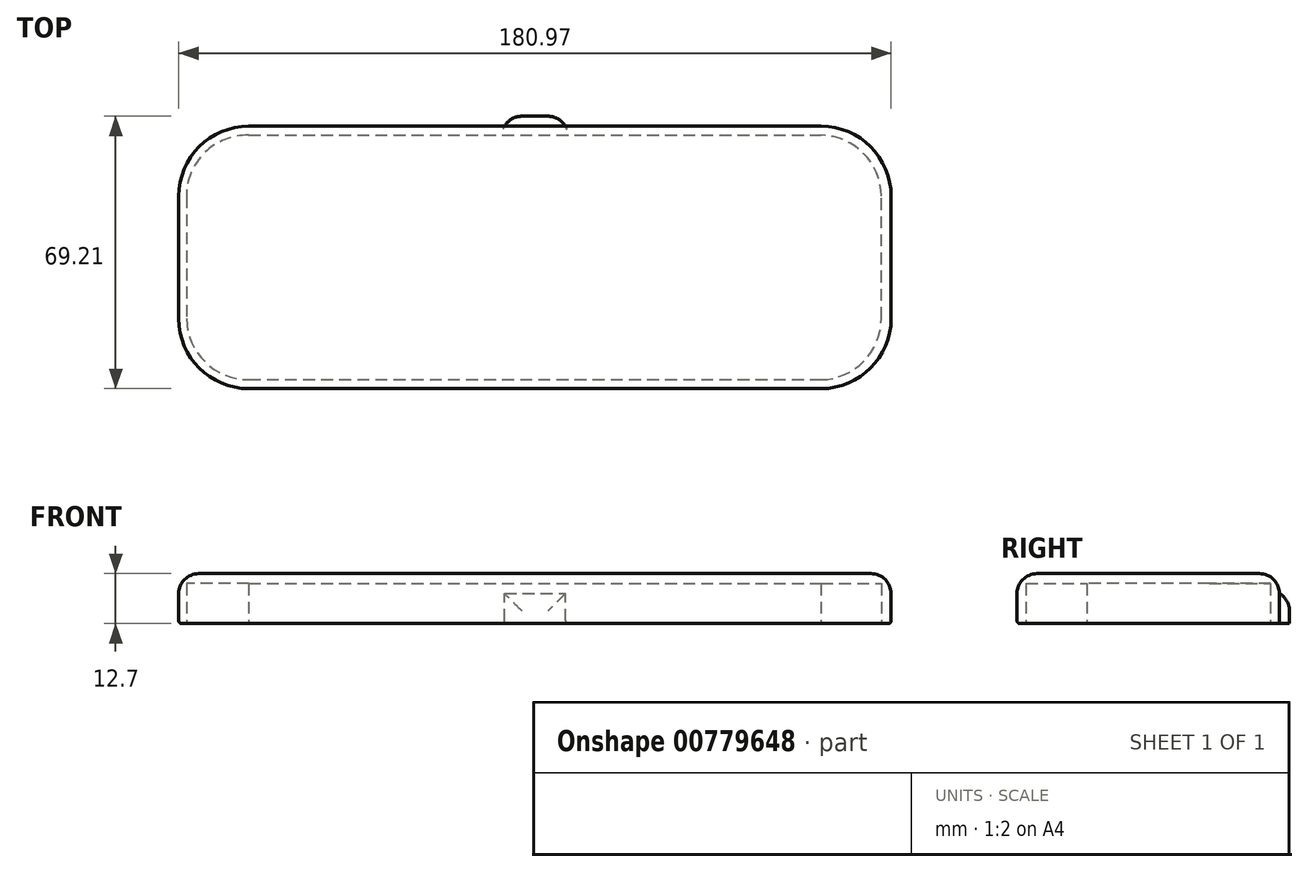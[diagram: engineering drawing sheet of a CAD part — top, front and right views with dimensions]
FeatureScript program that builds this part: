
annotation { "Feature Type Name" : "Feature", "Feature Type Description" : "" }
export const myFeature = defineFeature(function(context is Context, id is Id, definition is map)
    precondition{}
    {
        {
            var Q0;
            Q0=qCreatedBy(makeId("Top.planeOp"),FACE);
            var sketch = newSketch(context, id + "F0", { "sketchPlane" : qUnion([Q0])});
            skLineSegment(sketch, "E0.bottom", {"start": v(-69.58, 3.8) * mm, "end": v(111.4, 3.8) * mm});
            skLineSegment(sketch, "E0.top", {"start": v(-69.58, 70.48) * mm, "end": v(111.4, 70.48) * mm});
            skLineSegment(sketch, "E0.left", {"start": v(-69.58, 3.8) * mm, "end": v(-69.58, 70.48) * mm});
            skLineSegment(sketch, "E0.right", {"start": v(111.4, 3.8) * mm, "end": v(111.4, 70.48) * mm});
            skSolve(sketch);
        }
        {
            var Q0;
            Q0 = qSketchRegion(id + "F0", true);
            extrude(context, id + "F1", {"entities" : qUnion([Q0]), "depth" : 12.7 * mm, "offsetDistance" : 25.4 * mm});
        }
        {
            var Q0;
            Q0=makeQuery(id+"F1.opExtrude","SWEPT_EDGE",EDGE,{"disambiguationData":[OSD([sQuery(id+"F0.wireOp",EDGE,"E0.bottom"),sQuery(id+"F0.wireOp",EDGE,"E0.left")])]});
            var Q1;
            Q1=makeQuery(id+"F1.opExtrude","SWEPT_EDGE",EDGE,{"disambiguationData":[OSD([sQuery(id+"F0.wireOp",EDGE,"E0.bottom"),sQuery(id+"F0.wireOp",EDGE,"E0.right")])]});
            var Q2;
            Q2=makeQuery(id+"F1.opExtrude","SWEPT_EDGE",EDGE,{"disambiguationData":[OSD([sQuery(id+"F0.wireOp",EDGE,"E0.top"),sQuery(id+"F0.wireOp",EDGE,"E0.right")])]});
            var Q3;
            Q3=makeQuery(id+"F1.opExtrude","SWEPT_EDGE",EDGE,{"disambiguationData":[OSD([sQuery(id+"F0.wireOp",EDGE,"E0.top"),sQuery(id+"F0.wireOp",EDGE,"E0.left")])]});
            fillet(context, id + "F2", {"entities" : qUnion([Q0, Q1, Q2, Q3]), "radius" : 17.78 * mm, "tangentPropagation" : true, "allowEdgeOverflow" : false});
        }
        {
            var Q0;
            Q0=makeQuery(id+"F1.opExtrude","CAP_EDGE",EDGE,{"disambiguationData":[OSD([sQuery(id+"F0.wireOp",EDGE,"E0.bottom")])],"isStart":false});
            fillet(context, id + "F3", {"entities" : qUnion([Q0]), "radius" : 5.08 * mm, "tangentPropagation" : true, "allowEdgeOverflow" : false});
        }
        {
            var Q0;
            Q0=makeQuery(id+"F1.opExtrude","CAP_FACE",FACE,{"disambiguationData":[OSD([sQuery(id+"F0.wireOp",EDGE,"E0.bottom"),sQuery(id+"F0.wireOp",EDGE,"E0.top"),sQuery(id+"F0.wireOp",EDGE,"E0.left"),sQuery(id+"F0.wireOp",EDGE,"E0.right")])],"isStart":true});
            var sketch = newSketch(context, id + "F4", { "sketchPlane" : qUnion([Q0])});
            skLineSegment(sketch, "E1.bottom", {"start": v(-49.9, -68.2) * mm, "end": v(91.7, -68.2) * mm});
            skLineSegment(sketch, "E1.top", {"start": v(-49.9, -6.1) * mm, "end": v(91.7, -6.1) * mm});
            skLineSegment(sketch, "E1.left", {"start": v(-49.9, -68.2) * mm, "end": v(-49.9, -6.1) * mm});
            skLineSegment(sketch, "E1.right", {"start": v(91.7, -68.2) * mm, "end": v(91.7, -6.1) * mm});
            skPoint(sketch, "E1.middle", {"position": v(20.9, -37.14) * mm});
            skPoint(sketch, "E1.middle.positionSnap0", {"position": v(-69.58, -37.14) * mm});
            skPoint(sketch, "E1.middle.positionSnap1", {"position": v(20.9, -70.48) * mm});
            skPoint(sketch, "E1.centerSnap0", {"position": v(-69.58, -37.14) * mm});
            skPoint(sketch, "E1.centerSnap1", {"position": v(20.9, -70.48) * mm});
            skSolve(sketch);
        }
        {
            var Q0;
            Q0=makeQuery(id+"F4.imprint","IMPRINT",FACE,{"disambiguationData":[TD([[makeQuery(id+"F4.imprint","IMPRINT",EDGE,{"derivedFrom":sQuery(id+"F4.wireOp",EDGE,"E1.bottom")}),1.0]])]});
            extrude(context, id + "F5", {"entities" : qUnion([Q0]), "operationType" : NewBodyOperationType.REMOVE, "oppositeDirection" : true, "depth" : 10.16 * mm, "offsetDistance" : 25.4 * mm});
        }
        {
            var Q0;
            Q0=makeQuery(id+"F1.opExtrude","CAP_FACE",FACE,{"disambiguationData":[OSD([sQuery(id+"F0.wireOp",EDGE,"E0.bottom"),sQuery(id+"F0.wireOp",EDGE,"E0.top"),sQuery(id+"F0.wireOp",EDGE,"E0.left"),sQuery(id+"F0.wireOp",EDGE,"E0.right")])],"isStart":true});
            var sketch = newSketch(context, id + "F6", { "sketchPlane" : qUnion([Q0])});
            skLineSegment(sketch, "E2", {"start": v(91.7, -6.1) * mm, "end": v(93.61, -6.1) * mm});
            skLineSegment(sketch, "E3", {"start": v(93.61, -6.1) * mm, "end": v(108.88, -21.59) * mm});
            skLineSegment(sketch, "E4", {"start": v(108.88, -21.59) * mm, "end": v(108.88, -52.7) * mm});
            skLineSegment(sketch, "E5", {"start": v(108.88, -52.7) * mm, "end": v(93.61, -68.2) * mm});
            skLineSegment(sketch, "E6", {"start": v(93.61, -68.2) * mm, "end": v(91.7, -68.2) * mm});
            skSolve(sketch);
        }
        {
            var Q0;
            Q0 = qSketchRegion(id + "F6", true);
            var Q1;
            Q1=makeQuery(id+"F6.imprint","IMPRINT",FACE,{"disambiguationData":[TD([[makeQuery(id+"F6.imprint","IMPRINT",EDGE,{"derivedFrom":sQuery(id+"F6.wireOp",EDGE,"E2")}),-1.0]])]});
            extrude(context, id + "F7", {"entities" : qUnion([Q0, Q1]), "operationType" : NewBodyOperationType.REMOVE, "oppositeDirection" : true, "depth" : 10.16 * mm, "offsetDistance" : 25.4 * mm});
        }
        {
            var Q0;
            Q0=makeQuery(id+"F1.opExtrude","CAP_FACE",FACE,{"disambiguationData":[OSD([sQuery(id+"F0.wireOp",EDGE,"E0.bottom"),sQuery(id+"F0.wireOp",EDGE,"E0.top"),sQuery(id+"F0.wireOp",EDGE,"E0.left"),sQuery(id+"F0.wireOp",EDGE,"E0.right")])],"isStart":true});
            var sketch = newSketch(context, id + "F8", { "sketchPlane" : qUnion([Q0])});
            skArc(sketch, "E7", {"start": v(93.61, -68.2) * mm, "mid": v(104.42, -63.58) * mm, "end": v(108.88, -52.7) * mm});
            skSolve(sketch);
        }
        {
            var Q0;
            Q0=makeQuery(id+"F8.imprint","IMPRINT",FACE,{"disambiguationData":[TD([[makeQuery(id+"F8.imprint","IMPRINT",EDGE,{"derivedFrom":sQuery(id+"F8.wireOp",EDGE,"E7")}),1.0]])]});
            extrude(context, id + "F9", {"entities" : qUnion([Q0]), "operationType" : NewBodyOperationType.REMOVE, "oppositeDirection" : true, "depth" : 10.16 * mm, "offsetDistance" : 25.4 * mm});
        }
        {
            var Q0;
            Q0=makeQuery(id+"F1.opExtrude","CAP_FACE",FACE,{"disambiguationData":[OSD([sQuery(id+"F0.wireOp",EDGE,"E0.bottom"),sQuery(id+"F0.wireOp",EDGE,"E0.top"),sQuery(id+"F0.wireOp",EDGE,"E0.left"),sQuery(id+"F0.wireOp",EDGE,"E0.right")])],"isStart":true});
            var sketch = newSketch(context, id + "F10", { "sketchPlane" : qUnion([Q0])});
            skArc(sketch, "E8", {"start": v(108.88, -21.59) * mm, "mid": v(104.42, -10.71) * mm, "end": v(93.61, -6.1) * mm});
            skSolve(sketch);
        }
        {
            var Q0;
            Q0=makeQuery(id+"F10.imprint","IMPRINT",FACE,{"disambiguationData":[TD([[makeQuery(id+"F10.imprint","IMPRINT",EDGE,{"derivedFrom":sQuery(id+"F10.wireOp",EDGE,"E8")}),1.0]])]});
            extrude(context, id + "F11", {"entities" : qUnion([Q0]), "operationType" : NewBodyOperationType.REMOVE, "oppositeDirection" : true, "depth" : 10.16 * mm, "offsetDistance" : 25.4 * mm});
        }
        {
            var Q0;
            Q0=makeQuery(id+"F1.opExtrude","CAP_FACE",FACE,{"disambiguationData":[OSD([sQuery(id+"F0.wireOp",EDGE,"E0.bottom"),sQuery(id+"F0.wireOp",EDGE,"E0.top"),sQuery(id+"F0.wireOp",EDGE,"E0.left"),sQuery(id+"F0.wireOp",EDGE,"E0.right")])],"isStart":true});
            var sketch = newSketch(context, id + "F12", { "sketchPlane" : qUnion([Q0])});
            skLineSegment(sketch, "E9", {"start": v(-49.9, -68.2) * mm, "end": v(-51.8, -68.2) * mm});
            skLineSegment(sketch, "E10", {"start": v(-51.8, -68.2) * mm, "end": v(-67.63, -52.7) * mm});
            skLineSegment(sketch, "E11", {"start": v(-67.63, -52.7) * mm, "end": v(-67.63, -21.59) * mm});
            skLineSegment(sketch, "E12", {"start": v(-67.63, -21.59) * mm, "end": v(-51.8, -6.1) * mm});
            skLineSegment(sketch, "E13", {"start": v(-51.8, -6.1) * mm, "end": v(-49.9, -6.1) * mm});
            skSolve(sketch);
        }
        {
            var Q0;
            Q0=makeQuery(id+"F12.imprint","IMPRINT",FACE,{"disambiguationData":[TD([[makeQuery(id+"F12.imprint","IMPRINT",EDGE,{"derivedFrom":sQuery(id+"F12.wireOp",EDGE,"E9")}),-1.0]])]});
            extrude(context, id + "F13", {"entities" : qUnion([Q0]), "operationType" : NewBodyOperationType.REMOVE, "oppositeDirection" : true, "depth" : 10.16 * mm, "offsetDistance" : 25.4 * mm});
        }
        {
            var Q0;
            Q0=makeQuery(id+"F1.opExtrude","CAP_FACE",FACE,{"disambiguationData":[OSD([sQuery(id+"F0.wireOp",EDGE,"E0.bottom"),sQuery(id+"F0.wireOp",EDGE,"E0.top"),sQuery(id+"F0.wireOp",EDGE,"E0.left"),sQuery(id+"F0.wireOp",EDGE,"E0.right")])],"isStart":true});
            var sketch = newSketch(context, id + "F14", { "sketchPlane" : qUnion([Q0])});
            skArc(sketch, "E14", {"start": v(-67.63, -52.7) * mm, "mid": v(-62.97, -63.77) * mm, "end": v(-51.8, -68.2) * mm});
            skSolve(sketch);
        }
        {
            var Q0;
            Q0=makeQuery(id+"F14.imprint","IMPRINT",FACE,{"disambiguationData":[TD([[makeQuery(id+"F14.imprint","IMPRINT",EDGE,{"derivedFrom":sQuery(id+"F14.wireOp",EDGE,"E14")}),1.0]])]});
            extrude(context, id + "F15", {"entities" : qUnion([Q0]), "operationType" : NewBodyOperationType.REMOVE, "oppositeDirection" : true, "depth" : 10.16 * mm, "offsetDistance" : 25.4 * mm});
        }
        {
            var Q0;
            Q0=makeQuery(id+"F1.opExtrude","CAP_FACE",FACE,{"disambiguationData":[OSD([sQuery(id+"F0.wireOp",EDGE,"E0.bottom"),sQuery(id+"F0.wireOp",EDGE,"E0.top"),sQuery(id+"F0.wireOp",EDGE,"E0.left"),sQuery(id+"F0.wireOp",EDGE,"E0.right")])],"isStart":true});
            var sketch = newSketch(context, id + "F16", { "sketchPlane" : qUnion([Q0])});
            skArc(sketch, "E15", {"start": v(-51.8, -6.1) * mm, "mid": v(-62.87, -10.61) * mm, "end": v(-67.63, -21.59) * mm});
            skSolve(sketch);
        }
        {
            var Q0;
            Q0 = qSketchRegion(id + "F16", true);
            var Q1;
            Q1=makeQuery(id+"F16.imprint","IMPRINT",FACE,{"disambiguationData":[TD([[makeQuery(id+"F16.imprint","IMPRINT",EDGE,{"derivedFrom":sQuery(id+"F16.wireOp",EDGE,"E15")}),1.0]])]});
            extrude(context, id + "F17", {"entities" : qUnion([Q0, Q1]), "operationType" : NewBodyOperationType.REMOVE, "oppositeDirection" : true, "depth" : 10.16 * mm, "offsetDistance" : 25.4 * mm});
        }
        {
            var Q0;
            Q0=makeQuery(id+"F1.opExtrude","SWEPT_FACE",FACE,{"disambiguationData":[OSD([sQuery(id+"F0.wireOp",EDGE,"E0.top")])]});
            var sketch = newSketch(context, id + "F18", { "sketchPlane" : qUnion([Q0])});
            skLineSegment(sketch, "E16.bottom", {"start": v(-13.17, 0) * mm, "end": v(-28.64, 0) * mm});
            skLineSegment(sketch, "E16.top", {"start": v(-13.17, 7.62) * mm, "end": v(-28.64, 7.62) * mm});
            skLineSegment(sketch, "E16.left", {"start": v(-13.17, 0) * mm, "end": v(-13.17, 7.62) * mm});
            skLineSegment(sketch, "E16.right", {"start": v(-28.64, 0) * mm, "end": v(-28.64, 7.62) * mm});
            skPoint(sketch, "E16.middle", {"position": v(-20.9, 3.8) * mm});
            skPoint(sketch, "E16.middle.positionSnap0", {"position": v(51.8, 3.8) * mm});
            skPoint(sketch, "E16.middle.positionSnap1", {"position": v(-20.9, 0) * mm});
            skPoint(sketch, "E16.centerSnap0", {"position": v(51.8, 3.8) * mm});
            skPoint(sketch, "E16.centerSnap1", {"position": v(-20.9, 0) * mm});
            skSolve(sketch);
        }
        {
            var Q0;
            Q0 = qSketchRegion(id + "F18", true);
            extrude(context, id + "F19", {"entities" : qUnion([Q0]), "operationType" : NewBodyOperationType.ADD, "depth" : 2.54 * mm, "offsetDistance" : 25.4 * mm});
        }
        {
            var Q0;
            Q0=makeQuery(id+"F19.opExtrude","CAP_EDGE",EDGE,{"disambiguationData":[OSD([sQuery(id+"F18.wireOp",EDGE,"E16.right")])],"isStart":false});
            var Q1;
            Q1=makeQuery(id+"F19.opExtrude","CAP_EDGE",EDGE,{"disambiguationData":[OSD([sQuery(id+"F18.wireOp",EDGE,"E16.top")])],"isStart":false});
            var Q2;
            Q2=makeQuery(id+"F19.opExtrude","CAP_EDGE",EDGE,{"disambiguationData":[OSD([sQuery(id+"F18.wireOp",EDGE,"E16.left")])],"isStart":false});
            fillet(context, id + "F20", {"entities" : qUnion([Q0, Q1, Q2]), "radius" : 5.08 * mm, "tangentPropagation" : true, "allowEdgeOverflow" : false});
        }
        {
            var Q0;
            Q0=makeQuery(id+"F13.boolean.opBoolean","MERGE",EDGE,{"derivedFrom":[makeQuery(id+"F7.boolean.opBoolean","MERGE",EDGE,{"derivedFrom":[makeQuery(id+"F5.boolean.opBoolean","COPY",EDGE,{"derivedFrom":makeQuery(id+"F5.opExtrude","CAP_EDGE",EDGE,{"disambiguationData":[OSD([sQuery(id+"F4.wireOp",EDGE,"E1.top")])],"isStart":true})}),makeQuery(id+"F7.opExtrude","CAP_EDGE",EDGE,{"disambiguationData":[OSD([sQuery(id+"F6.wireOp",EDGE,"E2")])],"isStart":true})]}),makeQuery(id+"F13.opExtrude","CAP_EDGE",EDGE,{"disambiguationData":[OSD([sQuery(id+"F12.wireOp",EDGE,"E13")])],"isStart":true})]});
            var Q1;
            Q1=makeQuery(id+"F17.boolean.opBoolean","COPY",EDGE,{"derivedFrom":makeQuery(id+"F17.opExtrude","CAP_EDGE",EDGE,{"disambiguationData":[OSD([sQuery(id+"F16.wireOp",EDGE,"E15")])],"isStart":true})});
            var Q2;
            Q2=makeQuery(id+"F13.boolean.opBoolean","COPY",EDGE,{"derivedFrom":makeQuery(id+"F13.opExtrude","CAP_EDGE",EDGE,{"disambiguationData":[OSD([sQuery(id+"F12.wireOp",EDGE,"E11")])],"isStart":true})});
            var Q3;
            Q3=makeQuery(id+"F11.boolean.opBoolean","COPY",EDGE,{"derivedFrom":makeQuery(id+"F11.opExtrude","CAP_EDGE",EDGE,{"disambiguationData":[OSD([sQuery(id+"F10.wireOp",EDGE,"E8")])],"isStart":true})});
            var Q4;
            Q4=makeQuery(id+"F7.boolean.opBoolean","COPY",EDGE,{"derivedFrom":makeQuery(id+"F7.opExtrude","CAP_EDGE",EDGE,{"disambiguationData":[OSD([sQuery(id+"F6.wireOp",EDGE,"E4")])],"isStart":true})});
            var Q5;
            Q5=makeQuery(id+"F13.boolean.opBoolean","MERGE",EDGE,{"derivedFrom":[makeQuery(id+"F7.boolean.opBoolean","MERGE",EDGE,{"derivedFrom":[makeQuery(id+"F5.boolean.opBoolean","COPY",EDGE,{"derivedFrom":makeQuery(id+"F5.opExtrude","CAP_EDGE",EDGE,{"disambiguationData":[OSD([sQuery(id+"F4.wireOp",EDGE,"E1.bottom")])],"isStart":true})}),makeQuery(id+"F7.opExtrude","CAP_EDGE",EDGE,{"disambiguationData":[OSD([sQuery(id+"F6.wireOp",EDGE,"E6")])],"isStart":true})]}),makeQuery(id+"F13.opExtrude","CAP_EDGE",EDGE,{"disambiguationData":[OSD([sQuery(id+"F12.wireOp",EDGE,"E9")])],"isStart":true})]});
            var Q6;
            Q6=makeQuery(id+"F15.boolean.opBoolean","COPY",EDGE,{"derivedFrom":makeQuery(id+"F15.opExtrude","CAP_EDGE",EDGE,{"disambiguationData":[OSD([sQuery(id+"F14.wireOp",EDGE,"E14")])],"isStart":true})});
            var Q7;
            Q7=makeQuery(id+"F1.opExtrude","CAP_EDGE",EDGE,{"disambiguationData":[OSD([sQuery(id+"F0.wireOp",EDGE,"E0.bottom")])],"isStart":true});
            fillet(context, id + "F21", {"entities" : qUnion([Q0, Q1, Q2, Q3, Q4, Q5, Q6, Q7]), "radius" : 0.76 * mm, "tangentPropagation" : true, "allowEdgeOverflow" : false});
        }
    });
